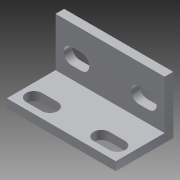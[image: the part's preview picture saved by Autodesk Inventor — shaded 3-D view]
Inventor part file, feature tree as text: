
AUTODESK INVENTOR PART (.ipt)
format: ipt  version: 2014 SP1 (Build 180222100, 222)  size: 131,072 bytes
history: native  units: in
note: dims shown in document units (in); Inventor stores cm internally (conversion verified against a paired STEP export)
features: extrude x3, sketch x3
ambient origin geometry x8: Origin, YZ Plane, XZ Plane, XY Plane, X Axis, Y Axis, Z Axis, Center Point
bodies: Solid1 (feature_tree)
feature tree (6):
  extrude  "Extrusion1"  Depth=1.4961in
  extrude  "Extrusion2"  Depth=0.2165in
  extrude  "Extrusion3"  Depth=0.1181in TaperAngle=0.0deg
  sketch  "Sketch1"  dims[d0=0.7874in d1=1.4961in]
  sketch  "Sketch2"  dims[d2=0.2165in d3=0.1378in]
  sketch  "Sketch3"  dims[d4=0.3937in d5=0.1181in d6=0.0in d7=0.1181in d8=0.6693in d9=0.0in d10=0.2165in d11=0.2165in d12=0.1969in d13=0.6693in d14=0.0in d15=0.9252in d16=0.9252in]
